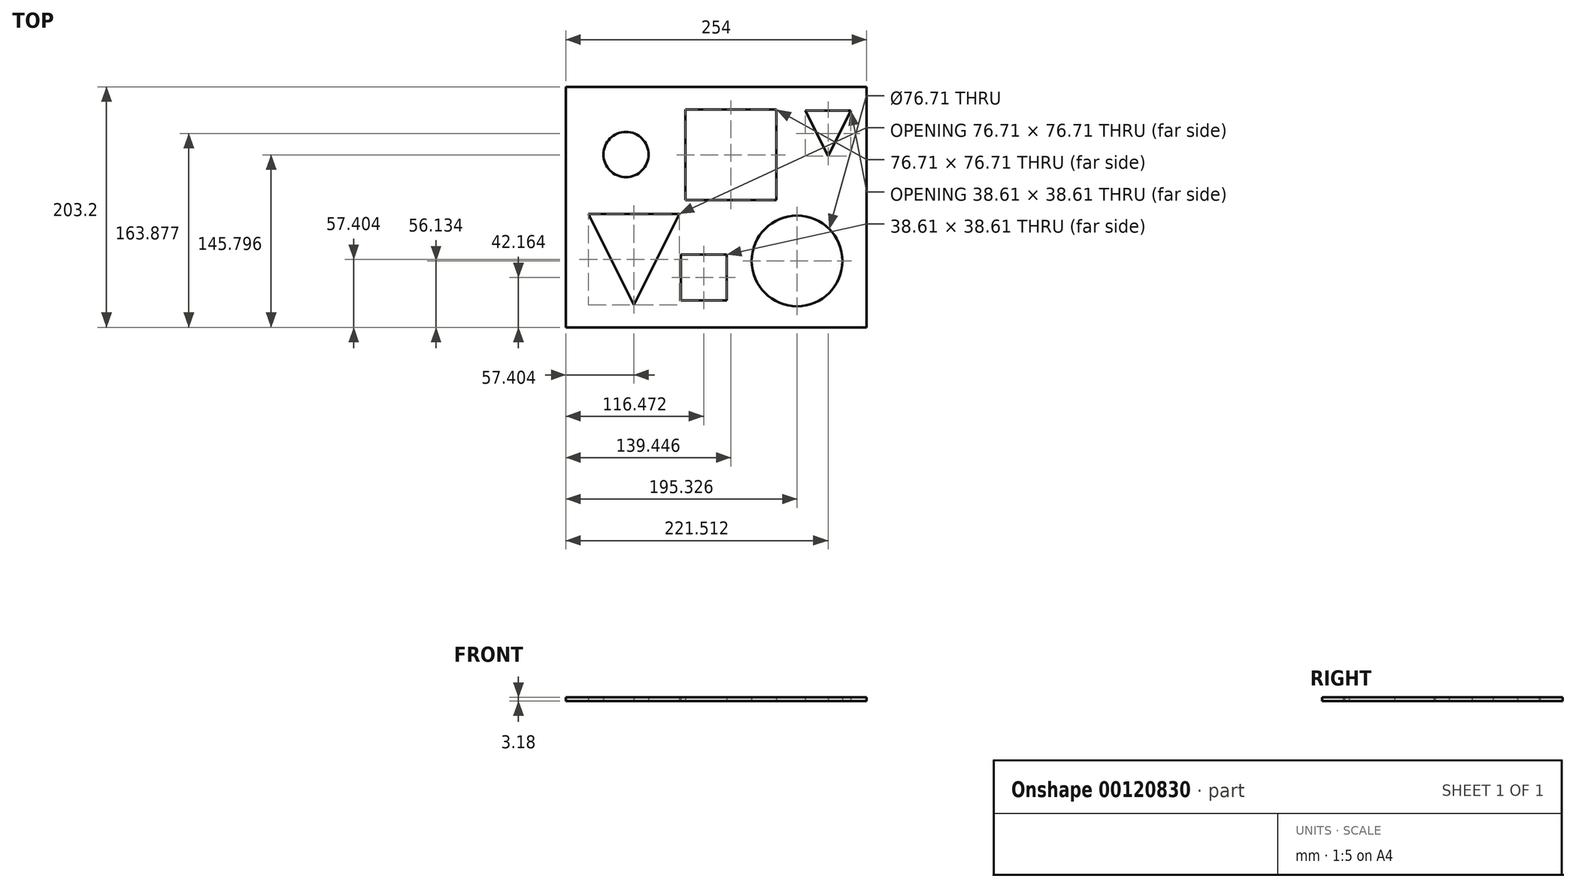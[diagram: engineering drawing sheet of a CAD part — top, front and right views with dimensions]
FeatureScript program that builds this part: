
annotation { "Feature Type Name" : "Feature", "Feature Type Description" : "" }
export const myFeature = defineFeature(function(context is Context, id is Id, definition is map)
    precondition{}
    {
        {
            var Q0;
            Q0=qCreatedBy(makeId("Top.planeOp"),FACE);
            var sketch = newSketch(context, id + "F0", { "sketchPlane" : qUnion([Q0])});
            skLineSegment(sketch, "E0.bottom", {"start": v(-127, 101.6) * mm, "end": v(127, 101.6) * mm});
            skLineSegment(sketch, "E0.top", {"start": v(-127, -101.6) * mm, "end": v(127, -101.6) * mm});
            skLineSegment(sketch, "E0.left", {"start": v(-127, 101.6) * mm, "end": v(-127, -101.6) * mm});
            skLineSegment(sketch, "E0.right", {"start": v(127, 101.6) * mm, "end": v(127, -101.6) * mm});
            skSolve(sketch);
        }
        {
            var Q0;
            Q0 = qSketchRegion(id + "F0", true);
            extrude(context, id + "F1", {"entities" : qUnion([Q0]), "depth" : 3.17 * mm});
        }
        {
            var Q0;
            Q0=makeQuery(id+"F1.opExtrude","CAP_FACE",FACE,{"disambiguationData":[OSD([sQuery(id+"F0.wireOp",EDGE,"E0.bottom"),sQuery(id+"F0.wireOp",EDGE,"E0.top"),sQuery(id+"F0.wireOp",EDGE,"E0.left"),sQuery(id+"F0.wireOp",EDGE,"E0.right")])],"isStart":true});
            var sketch = newSketch(context, id + "F2", { "sketchPlane" : qUnion([Q0])});
            skLineSegment(sketch, "E1", {"start": v(-107.95, 5.84) * mm, "end": v(-31.24, 5.84) * mm});
            skLineSegment(sketch, "E2", {"start": v(-69.6, 5.84) * mm, "end": v(-69.6, 82.55) * mm, "construction": true});
            skLineSegment(sketch, "E3", {"start": v(-107.95, 5.84) * mm, "end": v(-69.6, 82.55) * mm});
            skLineSegment(sketch, "E4", {"start": v(-69.6, 82.55) * mm, "end": v(-31.24, 5.84) * mm});
            skSolve(sketch);
        }
        {
            var Q0;
            Q0 = qSketchRegion(id + "F2", true);
            extrude(context, id + "F3", {"entities" : qUnion([Q0]), "operationType" : NewBodyOperationType.REMOVE, "oppositeDirection" : true, "depth" : 25.4 * mm});
        }
        {
            var Q0;
            Q0=makeQuery(id+"F1.opExtrude","CAP_FACE",FACE,{"disambiguationData":[OSD([sQuery(id+"F0.wireOp",EDGE,"E0.bottom"),sQuery(id+"F0.wireOp",EDGE,"E0.top"),sQuery(id+"F0.wireOp",EDGE,"E0.left"),sQuery(id+"F0.wireOp",EDGE,"E0.right")])],"isStart":true});
            var sketch = newSketch(context, id + "F4", { "sketchPlane" : qUnion([Q0])});
            skLineSegment(sketch, "E5.bottom", {"start": v(50.8, -82.55) * mm, "end": v(-25.9, -82.55) * mm});
            skLineSegment(sketch, "E5.top", {"start": v(50.8, -5.84) * mm, "end": v(-25.9, -5.84) * mm});
            skLineSegment(sketch, "E5.left", {"start": v(50.8, -82.55) * mm, "end": v(50.8, -5.84) * mm});
            skLineSegment(sketch, "E5.right", {"start": v(-25.9, -82.55) * mm, "end": v(-25.9, -5.84) * mm});
            skSolve(sketch);
        }
        {
            var Q0;
            Q0 = qSketchRegion(id + "F4", true);
            extrude(context, id + "F5", {"entities" : qUnion([Q0]), "operationType" : NewBodyOperationType.REMOVE, "oppositeDirection" : true, "depth" : 25.4 * mm});
        }
        {
            var Q0;
            Q0=makeQuery(id+"F1.opExtrude","CAP_FACE",FACE,{"disambiguationData":[OSD([sQuery(id+"F0.wireOp",EDGE,"E0.bottom"),sQuery(id+"F0.wireOp",EDGE,"E0.top"),sQuery(id+"F0.wireOp",EDGE,"E0.left"),sQuery(id+"F0.wireOp",EDGE,"E0.right")])],"isStart":true});
            var sketch = newSketch(context, id + "F6", { "sketchPlane" : qUnion([Q0])});
            skCircle(sketch, "E6", {"center": v(68.33, 45.47) * mm, "radius": 38.35 * mm});
            skSolve(sketch);
        }
        {
            var Q0;
            Q0 = qSketchRegion(id + "F6", true);
            extrude(context, id + "F7", {"entities" : qUnion([Q0]), "operationType" : NewBodyOperationType.REMOVE, "oppositeDirection" : true, "depth" : 25.4 * mm});
        }
        {
            var Q0;
            Q0=makeQuery(id+"F1.opExtrude","CAP_FACE",FACE,{"disambiguationData":[OSD([sQuery(id+"F0.wireOp",EDGE,"E0.bottom"),sQuery(id+"F0.wireOp",EDGE,"E0.top"),sQuery(id+"F0.wireOp",EDGE,"E0.left"),sQuery(id+"F0.wireOp",EDGE,"E0.right")])],"isStart":true});
            var sketch = newSketch(context, id + "F8", { "sketchPlane" : qUnion([Q0])});
            skLineSegment(sketch, "E7", {"start": v(75.2, -81.58) * mm, "end": v(113.82, -81.58) * mm});
            skLineSegment(sketch, "E8", {"start": v(94.51, -81.58) * mm, "end": v(94.51, -42.97) * mm, "construction": true});
            skLineSegment(sketch, "E9", {"start": v(75.2, -81.58) * mm, "end": v(94.51, -42.97) * mm});
            skLineSegment(sketch, "E10", {"start": v(113.82, -81.58) * mm, "end": v(94.51, -42.97) * mm});
            skSolve(sketch);
        }
        {
            var Q0;
            Q0 = qSketchRegion(id + "F8", true);
            extrude(context, id + "F9", {"entities" : qUnion([Q0]), "operationType" : NewBodyOperationType.REMOVE, "oppositeDirection" : true, "depth" : 25.4 * mm});
        }
        {
            var Q0;
            Q0=makeQuery(id+"F1.opExtrude","CAP_FACE",FACE,{"disambiguationData":[OSD([sQuery(id+"F0.wireOp",EDGE,"E0.bottom"),sQuery(id+"F0.wireOp",EDGE,"E0.top"),sQuery(id+"F0.wireOp",EDGE,"E0.left"),sQuery(id+"F0.wireOp",EDGE,"E0.right")])],"isStart":true});
            var sketch = newSketch(context, id + "F10", { "sketchPlane" : qUnion([Q0])});
            skCircle(sketch, "E11", {"center": v(-76.17, -44.42) * mm, "radius": 19.08 * mm});
            skSolve(sketch);
        }
        {
            var Q0;
            Q0 = qSketchRegion(id + "F10", true);
            extrude(context, id + "F11", {"entities" : qUnion([Q0]), "operationType" : NewBodyOperationType.REMOVE, "oppositeDirection" : true, "depth" : 25.4 * mm});
        }
        {
            var Q0;
            Q0=makeQuery(id+"F1.opExtrude","CAP_FACE",FACE,{"disambiguationData":[OSD([sQuery(id+"F0.wireOp",EDGE,"E0.bottom"),sQuery(id+"F0.wireOp",EDGE,"E0.top"),sQuery(id+"F0.wireOp",EDGE,"E0.left"),sQuery(id+"F0.wireOp",EDGE,"E0.right")])],"isStart":true});
            var sketch = newSketch(context, id + "F12", { "sketchPlane" : qUnion([Q0])});
            skLineSegment(sketch, "E12.bottom", {"start": v(-29.83, 78.74) * mm, "end": v(8.78, 78.74) * mm});
            skLineSegment(sketch, "E12.top", {"start": v(-29.83, 40.13) * mm, "end": v(8.78, 40.13) * mm});
            skLineSegment(sketch, "E12.left", {"start": v(-29.83, 78.74) * mm, "end": v(-29.83, 40.13) * mm});
            skLineSegment(sketch, "E12.right", {"start": v(8.78, 78.74) * mm, "end": v(8.78, 40.13) * mm});
            skSolve(sketch);
        }
        {
            var Q0;
            Q0 = qSketchRegion(id + "F12", true);
            extrude(context, id + "F13", {"entities" : qUnion([Q0]), "operationType" : NewBodyOperationType.REMOVE, "oppositeDirection" : true, "depth" : 25.4 * mm});
        }
    });
